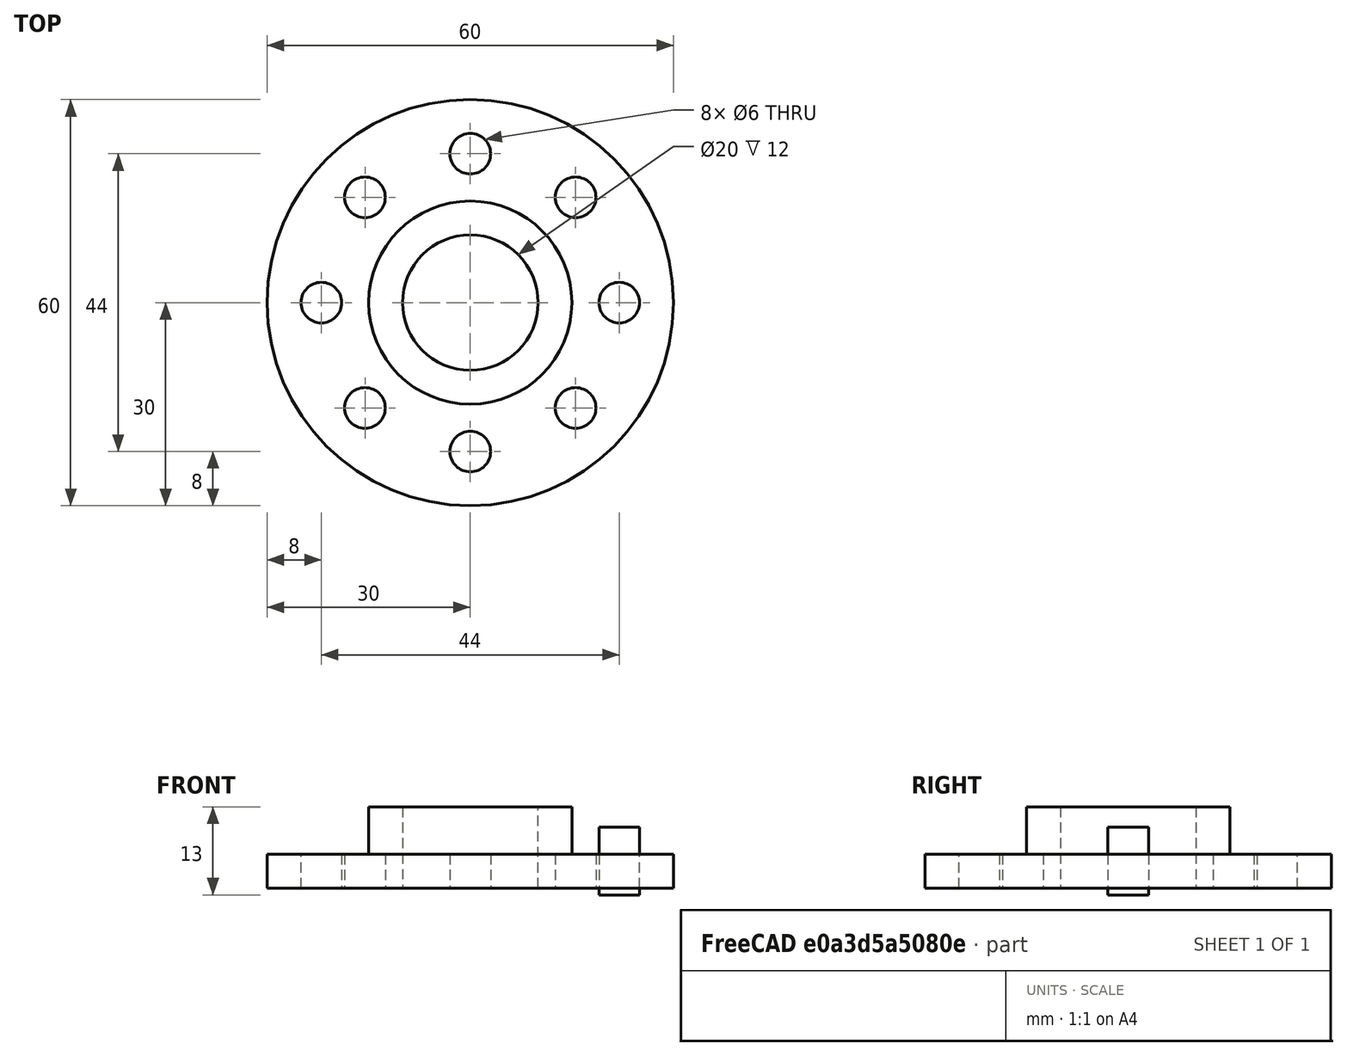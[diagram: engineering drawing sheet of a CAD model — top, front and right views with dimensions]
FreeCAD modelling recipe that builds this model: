
FCSTD DOCUMENT  (FreeCAD 1.0R39319 (Git))
Label: ojt1_t11p01_flange
License: All rights reserved
LicenseURL: https://en.wikipedia.org/wiki/All_rights_reserved
objects: Part::Cylinder×5, Part::Cut×2, Part::FeaturePython×2, Part::MultiFuse×1
note: 8 computed .brp shape members not serialized (recipe doc carries the construction recipe); baked Part::Feature solids carry a one-line shape summary decoded from their .brp

FEATURE [Part::Cylinder] Cylinder  label="base"
  Angle = 360
  AttacherType = Attacher::AttachEngine3D
  FirstAngle = 0
  Height = 5
  Radius = 30
  SecondAngle = 0
FEATURE [Part::Cylinder] Cylinder001  label="tubo exterior"
  Angle = 360
  AttacherType = Attacher::AttachEngine3D
  FirstAngle = 0
  Height = 12
  Radius = 15
  SecondAngle = 0
FEATURE [Part::MultiFuse] Fusion
  Refine = true
  Shapes = -> [Cylinder001,Cylinder]
FEATURE [Part::Cylinder] Cylinder002  label="tubo interior"
  Angle = 360
  AttacherType = Attacher::AttachEngine3D
  FirstAngle = 0
  Height = 30
  Placement = pos=(0,0,-1) rot=(0,0,1;0rad)
  Radius = 10
  SecondAngle = 0
FEATURE [Part::Cut] Cut  label="brida sin los taladros"
  Base = -> Fusion
  Refine = true
  Tool = -> Cylinder002
FEATURE [Part::Cylinder] Cylinder003  label="taladro master"
  Angle = 360
  AttacherType = Attacher::AttachEngine3D
  FirstAngle = 0
  Height = 10
  Placement = pos=(22,0,-1) rot=(0,0,1;0rad)
  Radius = 3
  SecondAngle = 0
FEATURE [Part::FeaturePython] Array  # Draft array (typed FeaturePython)
  AlwaysSyncPlacement = false
  Angle = 360
  ArrayType = 1
  Axis = (0,0,1)
  Base = -> Cylinder003
  Center = (0,0,0)
  Count = 8
  ExpandArray = false
  Fuse = false
  IntervalAxis = (0,0,0)
  IntervalX = (100,0,0)
  IntervalY = (0,100,0)
  IntervalZ = (0,0,100)
  NumberCircles = 3
  NumberPolar = 8
  NumberX = 2
  NumberY = 2
  NumberZ = 1
  PlacementList = 8 placements: [(22,0,-1),(15.5563,15.5563,-1),(0,22,-1),(-15.5563,15.5563,-1),(-22,2.69422e-15,-1),(-15.5563,-15.5563,-1),(-4.88498e-15,-22,-1),(15.5563,-15.5563,-1)]
  RadialDistance = 50
  ScaleList = (8) [(1,1,1),(1,1,1),(1,1,1),(1,1,1),(1,1,1),(1,1,1),(1,1,1),(1,1,1)]
  Symmetry = 1
  TangentialDistance = 25
FEATURE [Part::Cut] Cut001
  Base = -> Cut
  Refine = true
  Tool = -> Array
FEATURE [Part::Cylinder] Cylinder004  label="taladro master001"
  Angle = 360
  AttacherType = Attacher::AttachEngine3D
  FirstAngle = 0
  Height = 10
  Placement = pos=(22,0,-1) rot=(0,0,1;0rad)
  Radius = 3
  SecondAngle = 0
FEATURE [Part::FeaturePython] Array001  # Draft array (typed FeaturePython)
  AlwaysSyncPlacement = false
  Angle = 360
  ArrayType = 1
  Axis = (0,0,1)
  Base = -> Cylinder004
  Center = (0,0,0)
  Count = 8
  ExpandArray = false
  Fuse = false
  IntervalAxis = (0,0,0)
  IntervalX = (100,0,0)
  IntervalY = (0,100,0)
  IntervalZ = (0,0,100)
  NumberCircles = 3
  NumberPolar = 8
  NumberX = 2
  NumberY = 2
  NumberZ = 1
  PlacementList = 8 placements: [(22,0,-1),(15.5563,15.5563,-1),(0,22,-1),(-15.5563,15.5563,-1),(-22,2.69422e-15,-1),(-15.5563,-15.5563,-1),(-4.88498e-15,-22,-1),(15.5563,-15.5563,-1)]
  RadialDistance = 50
  ScaleList = (8) [(1,1,1),(1,1,1),(1,1,1),(1,1,1),(1,1,1),(1,1,1),(1,1,1),(1,1,1)]
  Symmetry = 1
  TangentialDistance = 25
